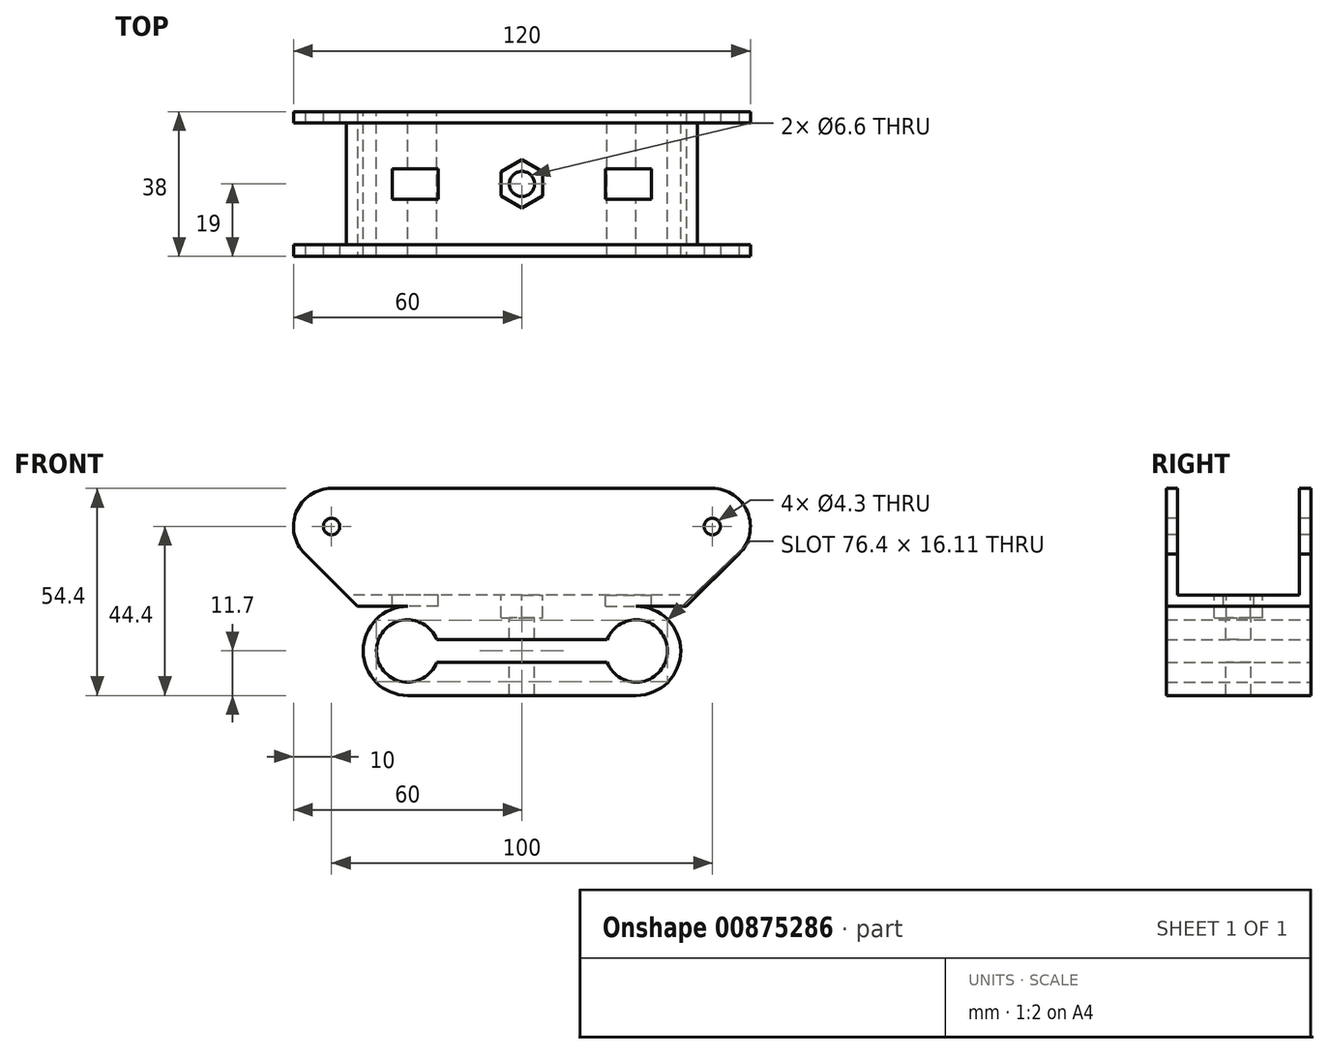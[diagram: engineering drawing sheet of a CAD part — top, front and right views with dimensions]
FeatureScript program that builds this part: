
annotation { "Feature Type Name" : "Feature", "Feature Type Description" : "" }
export const myFeature = defineFeature(function(context is Context, id is Id, definition is map)
    precondition{}
    {
        {
            var Q0;
            Q0=qCreatedBy(makeId("Front.planeOp"),FACE);
            var sketch = newSketch(context, id + "F0", { "sketchPlane" : qUnion([Q0])});
            skLineSegment(sketch, "E0.bottom", {"start": v(50, 18) * mm, "end": v(-50, 18) * mm, "construction": true});
            skPoint(sketch, "E0.middle", {"position": v(0, 18) * mm});
            skCircle(sketch, "E1", {"center": v(-50, 18) * mm, "radius": 2.15 * mm});
            skCircle(sketch, "E2", {"center": v(50, 18) * mm, "radius": 2.15 * mm});
            skSolve(sketch);
        }
        {
            var Q0;
            Q0=qCreatedBy(makeId("Right.planeOp"),FACE);
            var sketch = newSketch(context, id + "F1", { "sketchPlane" : qUnion([Q0])});
            skLineSegment(sketch, "E3.bottom", {"start": v(-16, 0) * mm, "end": v(16, 0) * mm});
            skLineSegment(sketch, "E4", {"start": v(16, 0) * mm, "end": v(16, 28) * mm});
            skLineSegment(sketch, "E5", {"start": v(-16, 0) * mm, "end": v(-16, 28) * mm});
            skLineSegment(sketch, "E6.0", {"start": v(19, -3) * mm, "end": v(19, 28) * mm});
            skLineSegment(sketch, "E6.1", {"start": v(-19, -3) * mm, "end": v(19, -3) * mm});
            skLineSegment(sketch, "E6.2", {"start": v(-19, -3) * mm, "end": v(-19, 28) * mm});
            skLineSegment(sketch, "E7", {"start": v(19, 28) * mm, "end": v(16, 28) * mm});
            skLineSegment(sketch, "E8", {"start": v(-16, 28) * mm, "end": v(-19, 28) * mm});
            skSolve(sketch);
        }
        {
            var Q0;
            Q0 = qSketchRegion(id + "F1", true);
            extrude(context, id + "F2", {"entities" : qUnion([Q0]), "endBound" : BoundingType.SYMMETRIC, "depth" : 120 * mm, "offsetDistance" : 25 * mm});
        }
        {
            var Q0;
            Q0=qCreatedBy(makeId("Front.planeOp"),FACE);
            var sketch = newSketch(context, id + "F3", { "sketchPlane" : qUnion([Q0])});
            skArc(sketch, "E9", {"start": v(-22.37, -11.7) * mm, "mid": v(-38.2, -14.7) * mm, "end": v(-22.37, -17.7) * mm});
            skArc(sketch, "E10.0", {"start": v(-30, -3) * mm, "mid": v(-41.7, -14.7) * mm, "end": v(-30, -26.4) * mm});
            skLineSegment(sketch, "E11", {"start": v(-30, -3) * mm, "end": v(0, -3) * mm});
            skLineSegment(sketch, "E12", {"start": v(-30, -26.4) * mm, "end": v(0, -26.4) * mm});
            skLineSegment(sketch, "E13.bottom", {"start": v(0, -17.7) * mm, "end": v(-22.37, -17.7) * mm});
            skLineSegment(sketch, "E13.top", {"start": v(0, -11.7) * mm, "end": v(-22.37, -11.7) * mm});
            skLineSegment(sketch, "E13.left", {"start": v(0, -17.7) * mm, "end": v(0, -11.7) * mm});
            skPoint(sketch, "E13.middle", {"position": v(-11.82, -14.7) * mm});
            skPoint(sketch, "E14.orphan", {"position": v(-23.63, -11.7) * mm});
            skPoint(sketch, "E15.orphan", {"position": v(-23.63, -17.7) * mm});
            skArc(sketch, "E16.MirrorCS", {"start": v(30, -3) * mm, "mid": v(41.7, -14.7) * mm, "end": v(30, -26.4) * mm});
            skPoint(sketch, "E17.MirrorP", {"position": v(23.63, -11.7) * mm});
            skLineSegment(sketch, "E18.MirrorCS", {"start": v(30, -3) * mm, "end": v(0, -3) * mm});
            skLineSegment(sketch, "E19.MirrorCS", {"start": v(0, -17.7) * mm, "end": v(22.37, -17.7) * mm});
            skPoint(sketch, "E20.MirrorP", {"position": v(23.63, -17.7) * mm});
            skLineSegment(sketch, "E21.MirrorCS", {"start": v(30, -26.4) * mm, "end": v(0, -26.4) * mm});
            skLineSegment(sketch, "E22.MirrorCS", {"start": v(0, -11.7) * mm, "end": v(22.37, -11.7) * mm});
            skPoint(sketch, "E23.MirrorP", {"position": v(11.82, -14.7) * mm});
            skArc(sketch, "E24.MirrorCS", {"start": v(22.37, -11.7) * mm, "mid": v(38.2, -14.7) * mm, "end": v(22.37, -17.7) * mm});
            skSolve(sketch);
        }
        {
            var Q0;
            Q0=makeQuery(id+"F3.imprint","IMPRINT",FACE,{"disambiguationData":[TD([[makeQuery(id+"F3.imprint","IMPRINT",EDGE,{"derivedFrom":sQuery(id+"F3.wireOp",EDGE,"E9")}),-1.0]])]});
            extrude(context, id + "F4", {"entities" : qUnion([Q0]), "operationType" : NewBodyOperationType.ADD, "endBound" : BoundingType.SYMMETRIC, "depth" : 38 * mm, "offsetDistance" : 25 * mm});
        }
        {
            var Q0;
            Q0 = qSketchRegion(id + "F0", true);
            extrude(context, id + "F5", {"entities" : qUnion([Q0]), "operationType" : NewBodyOperationType.REMOVE, "endBound" : BoundingType.SYMMETRIC, "oppositeDirection" : true, "depth" : 60.6 * mm, "offsetDistance" : 25 * mm});
        }
        {
            var Q0;
            Q0=makeQuery(id+"F2.opExtrude","CAP_EDGE",EDGE,{"disambiguationData":[OSD([sQuery(id+"F1.wireOp",EDGE,"E8")])],"isStart":true});
            var Q1;
            Q1=makeQuery(id+"F2.opExtrude","CAP_EDGE",EDGE,{"disambiguationData":[OSD([sQuery(id+"F1.wireOp",EDGE,"E7")])],"isStart":true});
            var Q2;
            Q2=makeQuery(id+"F2.opExtrude","CAP_EDGE",EDGE,{"disambiguationData":[OSD([sQuery(id+"F1.wireOp",EDGE,"E7")])],"isStart":false});
            var Q3;
            Q3=makeQuery(id+"F2.opExtrude","CAP_EDGE",EDGE,{"disambiguationData":[OSD([sQuery(id+"F1.wireOp",EDGE,"E8")])],"isStart":false});
            fillet(context, id + "F6", {"entities" : qUnion([Q0, Q1, Q2, Q3]), "radius" : 10 * mm, "tangentPropagation" : true, "allowEdgeOverflow" : false});
        }
        {
            var Q0;
            Q0=qCreatedBy(makeId("Top.planeOp"),FACE);
            var sketch = newSketch(context, id + "F7", { "sketchPlane" : qUnion([Q0])});
            skCircle(sketch, "E25", {"center": v(0, 0) * mm, "radius": 3.3 * mm});
            skSolve(sketch);
        }
        {
            var Q0;
            Q0 = qSketchRegion(id + "F7", true);
            extrude(context, id + "F8", {"entities" : qUnion([Q0]), "operationType" : NewBodyOperationType.REMOVE, "endBound" : BoundingType.SYMMETRIC, "oppositeDirection" : true, "depth" : 59 * mm, "offsetDistance" : 25 * mm});
        }
        {
            var Q0;
            Q0=qCreatedBy(makeId("Top.planeOp"),FACE);
            var sketch = newSketch(context, id + "F9", { "sketchPlane" : qUnion([Q0])});
            skCircle(sketch, "E26.cCircle", {"center": v(0, 0) * mm, "radius": 5.5 * mm, "construction": true});
            skLineSegment(sketch, "E26.0", {"start": v(5.5, 3.18) * mm, "end": v(5.5, -3.18) * mm});
            skLineSegment(sketch, "E26.1", {"start": v(5.5, -3.18) * mm, "end": v(0, -6.35) * mm});
            skLineSegment(sketch, "E26.2", {"start": v(0, -6.35) * mm, "end": v(-5.5, -3.18) * mm});
            skLineSegment(sketch, "E26.3", {"start": v(-5.5, -3.18) * mm, "end": v(-5.5, 3.18) * mm});
            skLineSegment(sketch, "E26.4", {"start": v(-5.5, 3.18) * mm, "end": v(0, 6.35) * mm});
            skLineSegment(sketch, "E26.5", {"start": v(0, 6.35) * mm, "end": v(5.5, 3.18) * mm});
            skPoint(sketch, "E26.0.midPoint", {"position": v(5.5, 0) * mm});
            skLineSegment(sketch, "E27.bottom", {"start": v(-22, -4) * mm, "end": v(-34, -4) * mm});
            skLineSegment(sketch, "E27.top", {"start": v(-22, 4) * mm, "end": v(-34, 4) * mm});
            skLineSegment(sketch, "E27.left", {"start": v(-22, -4) * mm, "end": v(-22, 4) * mm});
            skLineSegment(sketch, "E27.right", {"start": v(-34, -4) * mm, "end": v(-34, 4) * mm});
            skPoint(sketch, "E27.middle", {"position": v(-28, 0) * mm});
            skLineSegment(sketch, "E28.MirrorCS", {"start": v(22, -4) * mm, "end": v(34, -4) * mm});
            skLineSegment(sketch, "E29.MirrorCS", {"start": v(34, -4) * mm, "end": v(34, 4) * mm});
            skLineSegment(sketch, "E30.MirrorCS", {"start": v(22, -4) * mm, "end": v(22, 4) * mm});
            skLineSegment(sketch, "E31.MirrorCS", {"start": v(22, 4) * mm, "end": v(34, 4) * mm});
            skSolve(sketch);
        }
        {
            var Q0;
            Q0=makeQuery(id+"F9.imprint","IMPRINT",FACE,{"disambiguationData":[TD([[makeQuery(id+"F9.imprint","IMPRINT",EDGE,{"derivedFrom":sQuery(id+"F9.wireOp",EDGE,"E26.0")}),-1.0]])]});
            extrude(context, id + "F10", {"entities" : qUnion([Q0]), "operationType" : NewBodyOperationType.REMOVE, "oppositeDirection" : true, "depth" : 6 * mm, "offsetDistance" : 25 * mm});
        }
        {
            var Q0;
            Q0=makeQuery(id+"F9.imprint","IMPRINT",FACE,{"disambiguationData":[TD([[makeQuery(id+"F9.imprint","IMPRINT",EDGE,{"derivedFrom":sQuery(id+"F9.wireOp",EDGE,"E27.bottom")}),-1.0]])]});
            var Q1;
            Q1=makeQuery(id+"F9.imprint","IMPRINT",FACE,{"disambiguationData":[TD([[makeQuery(id+"F9.imprint","IMPRINT",EDGE,{"derivedFrom":sQuery(id+"F9.wireOp",EDGE,"E28.MirrorCS")}),1.0]])]});
            extrude(context, id + "F11", {"entities" : qUnion([Q0, Q1]), "operationType" : NewBodyOperationType.REMOVE, "oppositeDirection" : true, "depth" : 3 * mm, "offsetDistance" : 25 * mm});
        }
        {
            var Q0;
            Q0=qCreatedBy(makeId("Front.planeOp"),FACE);
            var sketch = newSketch(context, id + "F12", { "sketchPlane" : qUnion([Q0])});
            skArc(sketch, "E32", {"start": v(-58.7, 22.94) * mm, "mid": v(-59.9, 16.59) * mm, "end": v(-56.97, 10.83) * mm});
            skLineSegment(sketch, "E33", {"start": v(-57.07, 10.93) * mm, "end": v(-43.14, -3) * mm});
            skLineSegment(sketch, "E34", {"start": v(0, -3) * mm, "end": v(-43.14, -3) * mm});
            skLineSegment(sketch, "E35", {"start": v(-58.7, 22.94) * mm, "end": v(-66.43, 22.94) * mm});
            skLineSegment(sketch, "E36", {"start": v(-66.43, 22.94) * mm, "end": v(-66.43, -3) * mm});
            skLineSegment(sketch, "E37", {"start": v(-66.43, -3) * mm, "end": v(0, -3) * mm});
            skLineSegment(sketch, "E38", {"start": v(0, -3) * mm, "end": v(0, -3) * mm});
            skLineSegment(sketch, "E39.MirrorCS", {"start": v(58.7, 22.94) * mm, "end": v(66.43, 22.94) * mm});
            skLineSegment(sketch, "E40.MirrorCS", {"start": v(0, -3) * mm, "end": v(43.14, -3) * mm});
            skLineSegment(sketch, "E41.MirrorCS", {"start": v(66.43, 22.94) * mm, "end": v(66.43, -3) * mm});
            skLineSegment(sketch, "E42.MirrorCS", {"start": v(57.07, 10.93) * mm, "end": v(43.14, -3) * mm});
            skLineSegment(sketch, "E43.MirrorCS", {"start": v(66.43, -3) * mm, "end": v(0, -3) * mm});
            skArc(sketch, "E44.MirrorC", {"start": v(58.7, 22.94) * mm, "mid": v(59.9, 16.59) * mm, "end": v(56.97, 10.83) * mm});
            skSolve(sketch);
        }
        {
            var Q0;
            Q0 = qSketchRegion(id + "F12", true);
            extrude(context, id + "F13", {"entities" : qUnion([Q0]), "operationType" : NewBodyOperationType.REMOVE, "endBound" : BoundingType.SYMMETRIC, "oppositeDirection" : true, "depth" : 50 * mm, "offsetDistance" : 25 * mm});
        }
    });
